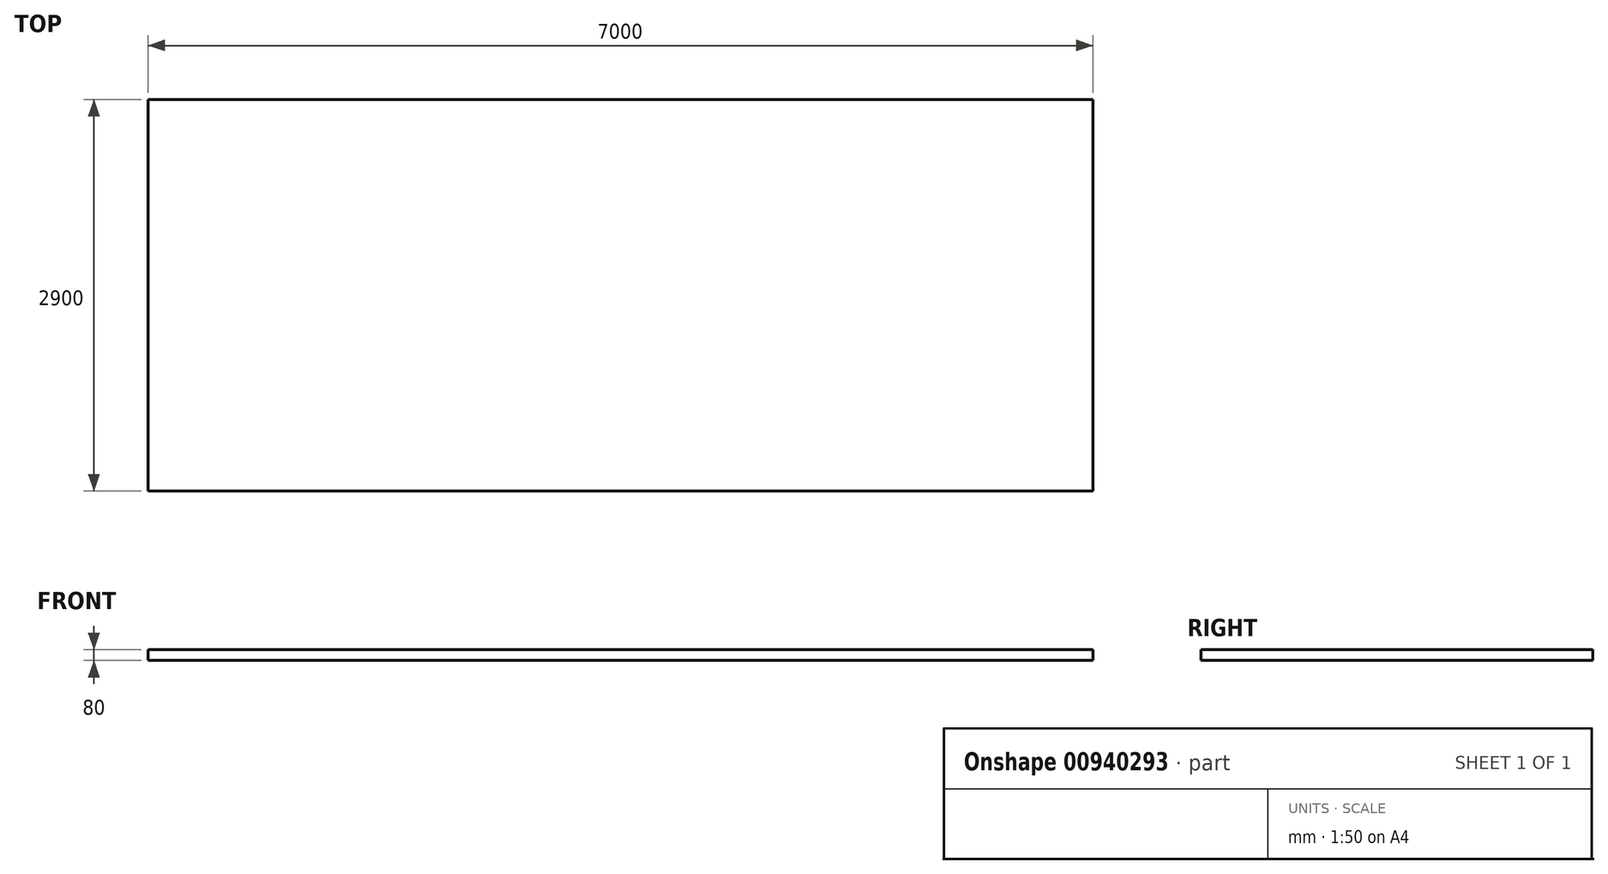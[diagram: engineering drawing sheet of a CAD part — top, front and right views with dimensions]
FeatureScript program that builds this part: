
annotation { "Feature Type Name" : "Feature", "Feature Type Description" : "" }
export const myFeature = defineFeature(function(context is Context, id is Id, definition is map)
    precondition{}
    {
        {
            var Q0;
            Q0=qCreatedBy(makeId("Top.planeOp"),FACE);
            var sketch = newSketch(context, id + "F0", { "sketchPlane" : qUnion([Q0])});
            skLineSegment(sketch, "E0.bottom", {"start": v(-3500, 1450) * mm, "end": v(3500, 1450) * mm});
            skLineSegment(sketch, "E0.top", {"start": v(-3500, -1450) * mm, "end": v(3500, -1450) * mm});
            skLineSegment(sketch, "E0.left", {"start": v(-3500, 1450) * mm, "end": v(-3500, -1450) * mm});
            skLineSegment(sketch, "E0.right", {"start": v(3500, 1450) * mm, "end": v(3500, -1450) * mm});
            skSolve(sketch);
        }
        {
            var Q0;
            Q0 = qSketchRegion(id + "F0", true);
            extrude(context, id + "F1", {"entities" : qUnion([Q0]), "depth" : 80 * mm, "offsetDistance" : 25 * mm});
        }
    });
